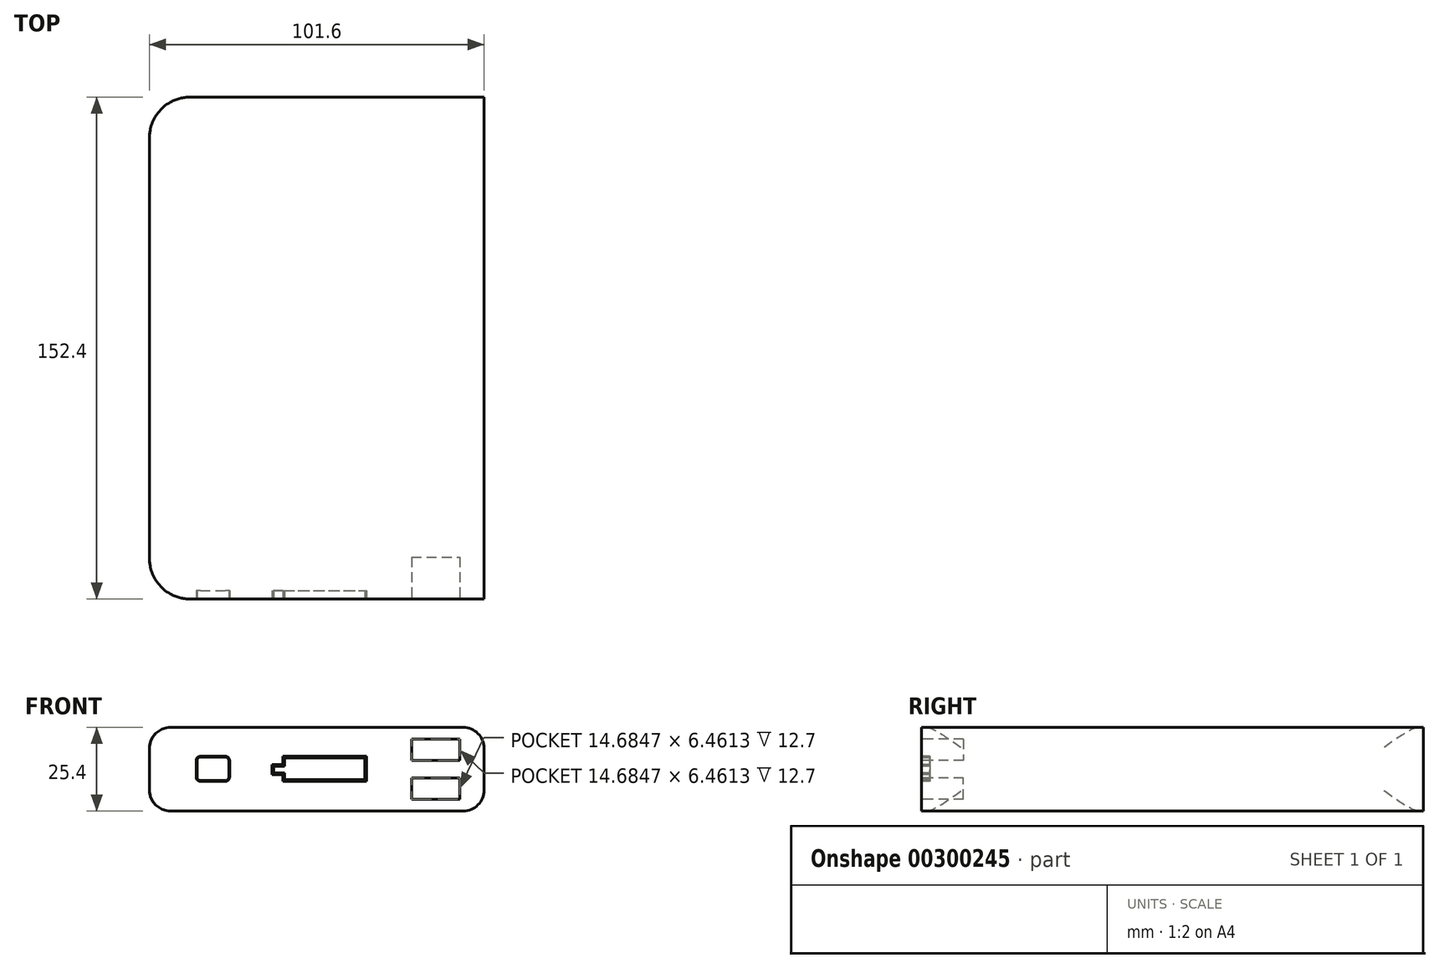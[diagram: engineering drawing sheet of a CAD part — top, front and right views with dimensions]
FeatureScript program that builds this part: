
annotation { "Feature Type Name" : "Feature", "Feature Type Description" : "" }
export const myFeature = defineFeature(function(context is Context, id is Id, definition is map)
    precondition{}
    {
        {
            var Q0;
            Q0=qCreatedBy(makeId("Front.planeOp"),FACE);
            var sketch = newSketch(context, id + "F0", { "sketchPlane" : qUnion([Q0])});
            skLineSegment(sketch, "E0", {"start": v(0, 6.35) * mm, "end": v(0, 19.05) * mm});
            skLineSegment(sketch, "E1", {"start": v(6.35, 25.4) * mm, "end": v(95.25, 25.4) * mm});
            skLineSegment(sketch, "E2", {"start": v(101.6, 19.05) * mm, "end": v(101.6, 6.35) * mm});
            skLineSegment(sketch, "E3", {"start": v(95.25, 0) * mm, "end": v(6.35, 0) * mm});
            skPoint(sketch, "E4.visualSharp", {"position": v(101.6, 25.4) * mm});
            skArc(sketch, "E4.filletArc", {"start": v(101.6, 19.05) * mm, "mid": v(99.74, 23.54) * mm, "end": v(95.25, 25.4) * mm});
            skPoint(sketch, "E5.visualSharp", {"position": v(101.6, 0) * mm});
            skArc(sketch, "E5.filletArc", {"start": v(95.25, 0) * mm, "mid": v(99.74, 1.86) * mm, "end": v(101.6, 6.35) * mm});
            skPoint(sketch, "E6.visualSharp", {"position": v(0, 25.4) * mm});
            skArc(sketch, "E6.filletArc", {"start": v(6.35, 25.4) * mm, "mid": v(1.86, 23.54) * mm, "end": v(0, 19.05) * mm});
            skPoint(sketch, "E7.visualSharp", {"position": v(0, 0) * mm});
            skArc(sketch, "E7.filletArc", {"start": v(0, 6.35) * mm, "mid": v(1.86, 1.86) * mm, "end": v(6.35, 0) * mm});
            skSolve(sketch);
        }
        {
            var Q0;
            Q0=makeQuery(id+"F0.imprint","IMPRINT",FACE,{"disambiguationData":[TD([[makeQuery(id+"F0.imprint","IMPRINT",EDGE,{"derivedFrom":sQuery(id+"F0.wireOp",EDGE,"E0")}),-1.0]])]});
            extrude(context, id + "F1", {"entities" : qUnion([Q0]), "depth" : 152.4 * mm});
        }
        {
            var Q0;
            Q0=makeQuery(id+"F1.opExtrude","CAP_EDGE",EDGE,{"disambiguationData":[OSD([sQuery(id+"F0.wireOp",EDGE,"E0")])],"isStart":false});
            fillet(context, id + "F2", {"entities" : qUnion([Q0]), "radius" : 12.26 * mm, "allowEdgeOverflow" : false});
        }
        {
            var Q0;
            Q0=makeQuery(id+"F1.opExtrude","CAP_EDGE",EDGE,{"disambiguationData":[OSD([sQuery(id+"F0.wireOp",EDGE,"E0")])],"isStart":true});
            fillet(context, id + "F3", {"entities" : qUnion([Q0]), "radius" : 12.27 * mm, "allowEdgeOverflow" : false});
        }
        {
            var Q0;
            Q0=makeQuery(id+"F1.opExtrude","CAP_FACE",FACE,{"disambiguationData":[OSD([sQuery(id+"F0.wireOp",EDGE,"E0"),sQuery(id+"F0.wireOp",EDGE,"E1"),sQuery(id+"F0.wireOp",EDGE,"E2"),sQuery(id+"F0.wireOp",EDGE,"E3"),sQuery(id+"F0.wireOp",EDGE,"E4.filletArc"),sQuery(id+"F0.wireOp",EDGE,"E5.filletArc"),sQuery(id+"F0.wireOp",EDGE,"E6.filletArc"),sQuery(id+"F0.wireOp",EDGE,"E7.filletArc")])],"isStart":false});
            var sketch = newSketch(context, id + "F4", { "sketchPlane" : qUnion([Q0])});
            skLineSegment(sketch, "E8.bottom", {"start": v(79.56, 21.8) * mm, "end": v(94.25, 21.8) * mm});
            skLineSegment(sketch, "E8.top", {"start": v(79.56, 15.34) * mm, "end": v(94.25, 15.34) * mm});
            skLineSegment(sketch, "E8.left", {"start": v(79.56, 21.8) * mm, "end": v(79.56, 15.34) * mm});
            skLineSegment(sketch, "E8.right", {"start": v(94.25, 21.8) * mm, "end": v(94.25, 15.34) * mm});
            skLineSegment(sketch, "E9.MirrorCS", {"start": v(79.56, 3.6) * mm, "end": v(94.25, 3.6) * mm});
            skLineSegment(sketch, "E10.MirrorCS", {"start": v(79.56, 3.6) * mm, "end": v(79.56, 10.06) * mm});
            skLineSegment(sketch, "E11.MirrorCS", {"start": v(79.56, 10.06) * mm, "end": v(94.25, 10.06) * mm});
            skLineSegment(sketch, "E12.MirrorCS", {"start": v(94.25, 3.6) * mm, "end": v(94.25, 10.06) * mm});
            skSolve(sketch);
        }
        {
            var Q0;
            Q0=makeQuery(id+"F4.imprint","IMPRINT",FACE,{"disambiguationData":[TD([[makeQuery(id+"F4.imprint","IMPRINT",EDGE,{"derivedFrom":sQuery(id+"F4.wireOp",EDGE,"E8.bottom")}),-1.0]])]});
            var Q1;
            Q1=makeQuery(id+"F4.imprint","IMPRINT",FACE,{"disambiguationData":[TD([[makeQuery(id+"F4.imprint","IMPRINT",EDGE,{"derivedFrom":sQuery(id+"F4.wireOp",EDGE,"E9.MirrorCS")}),1.0]])]});
            extrude(context, id + "F5", {"entities" : qUnion([Q0, Q1]), "operationType" : NewBodyOperationType.REMOVE, "oppositeDirection" : true, "depth" : 12.7 * mm});
        }
        {
            var Q0;
            Q0=makeQuery(id+"F1.opExtrude","CAP_FACE",FACE,{"disambiguationData":[OSD([sQuery(id+"F0.wireOp",EDGE,"E0"),sQuery(id+"F0.wireOp",EDGE,"E1"),sQuery(id+"F0.wireOp",EDGE,"E2"),sQuery(id+"F0.wireOp",EDGE,"E3"),sQuery(id+"F0.wireOp",EDGE,"E4.filletArc"),sQuery(id+"F0.wireOp",EDGE,"E5.filletArc"),sQuery(id+"F0.wireOp",EDGE,"E6.filletArc"),sQuery(id+"F0.wireOp",EDGE,"E7.filletArc")])],"isStart":false});
            var sketch = newSketch(context, id + "F6", { "sketchPlane" : qUnion([Q0])});
            skLineSegment(sketch, "E13", {"start": v(37.21, 14.1) * mm, "end": v(37.21, 11.05) * mm});
            skLineSegment(sketch, "E14", {"start": v(37.21, 11.05) * mm, "end": v(40.52, 11.05) * mm});
            skLineSegment(sketch, "E15", {"start": v(40.52, 11.05) * mm, "end": v(40.52, 9) * mm});
            skLineSegment(sketch, "E16", {"start": v(40.52, 9) * mm, "end": v(65.92, 9) * mm});
            skLineSegment(sketch, "E17", {"start": v(65.92, 9) * mm, "end": v(65.92, 16.63) * mm});
            skLineSegment(sketch, "E18", {"start": v(65.92, 16.63) * mm, "end": v(40.52, 16.63) * mm});
            skLineSegment(sketch, "E19", {"start": v(40.52, 16.63) * mm, "end": v(40.52, 14.1) * mm});
            skLineSegment(sketch, "E20", {"start": v(40.52, 14.1) * mm, "end": v(37.21, 14.1) * mm});
            skLineSegment(sketch, "E21.0", {"start": v(65.4, 9.51) * mm, "end": v(65.4, 16.12) * mm});
            skLineSegment(sketch, "E21.1", {"start": v(41.02, 9.51) * mm, "end": v(65.4, 9.51) * mm});
            skLineSegment(sketch, "E21.2", {"start": v(65.4, 16.12) * mm, "end": v(41.02, 16.12) * mm});
            skLineSegment(sketch, "E21.3", {"start": v(41.02, 11.56) * mm, "end": v(41.02, 9.51) * mm});
            skLineSegment(sketch, "E21.4", {"start": v(41.02, 16.12) * mm, "end": v(41.02, 13.59) * mm});
            skLineSegment(sketch, "E21.5", {"start": v(41.02, 13.59) * mm, "end": v(37.72, 13.59) * mm});
            skLineSegment(sketch, "E21.6", {"start": v(37.72, 13.59) * mm, "end": v(37.72, 11.56) * mm});
            skLineSegment(sketch, "E21.7", {"start": v(37.72, 11.56) * mm, "end": v(41.02, 11.56) * mm});
            skSolve(sketch);
        }
        {
            var Q0;
            Q0 = qSketchRegion(id + "F6", true);
            extrude(context, id + "F7", {"entities" : qUnion([Q0]), "operationType" : NewBodyOperationType.REMOVE, "oppositeDirection" : true, "depth" : 2.54 * mm});
        }
        {
            var Q0;
            {var subQ0=sQuery(id+"F0.wireOp",EDGE,"E5.filletArc");var subQ1=sQuery(id+"F0.wireOp",EDGE,"E1");var subQ2=sQuery(id+"F0.wireOp",EDGE,"E0");var subQ3=sQuery(id+"F0.wireOp",EDGE,"E2");var subQ4=sQuery(id+"F0.wireOp",EDGE,"E3");var subQ5=sQuery(id+"F0.wireOp",EDGE,"E4.filletArc");Q0=makeQuery(id+"F7.boolean.opBoolean","SPLIT",FACE,{"disambiguationData":[TD([makeQuery(id+"F1.opExtrude","SWEPT_FACE",FACE,{"disambiguationData":[OSD([subQ1])]})])],"derivedFrom":makeQuery(id+"F1.opExtrude","CAP_FACE",FACE,{"disambiguationData":[OSD([subQ2,subQ1,subQ3,subQ4,subQ5,subQ0,sQuery(id+"F0.wireOp",EDGE,"E6.filletArc"),sQuery(id+"F0.wireOp",EDGE,"E7.filletArc")])],"isStart":false})});}
            var sketch = newSketch(context, id + "F8", { "sketchPlane" : qUnion([Q0])});
            skLineSegment(sketch, "E22.bottom", {"start": v(15.44, 16.63) * mm, "end": v(23.06, 16.63) * mm});
            skLineSegment(sketch, "E22.top", {"start": v(15.44, 9) * mm, "end": v(23.06, 9) * mm});
            skLineSegment(sketch, "E22.left", {"start": v(14.17, 15.36) * mm, "end": v(14.17, 10.28) * mm});
            skLineSegment(sketch, "E22.right", {"start": v(24.33, 15.36) * mm, "end": v(24.33, 10.28) * mm});
            skPoint(sketch, "E23.visualSharp", {"position": v(14.17, 16.63) * mm});
            skArc(sketch, "E23.filletArc", {"start": v(15.44, 16.63) * mm, "mid": v(14.54, 16.25) * mm, "end": v(14.17, 15.36) * mm});
            skPoint(sketch, "E24.visualSharp", {"position": v(24.33, 16.63) * mm});
            skArc(sketch, "E24.filletArc", {"start": v(24.33, 15.36) * mm, "mid": v(23.96, 16.25) * mm, "end": v(23.06, 16.63) * mm});
            skPoint(sketch, "E25.visualSharp", {"position": v(24.33, 9) * mm});
            skArc(sketch, "E25.filletArc", {"start": v(23.06, 9) * mm, "mid": v(23.96, 9.38) * mm, "end": v(24.33, 10.28) * mm});
            skPoint(sketch, "E26.visualSharp", {"position": v(14.17, 9) * mm});
            skArc(sketch, "E26.filletArc", {"start": v(14.17, 10.28) * mm, "mid": v(14.54, 9.38) * mm, "end": v(15.44, 9) * mm});
            skArc(sketch, "E27.0", {"start": v(15.44, 16.36) * mm, "mid": v(14.72, 16.07) * mm, "end": v(14.43, 15.36) * mm});
            skLineSegment(sketch, "E27.1", {"start": v(14.43, 15.36) * mm, "end": v(14.43, 10.28) * mm});
            skLineSegment(sketch, "E27.2", {"start": v(15.44, 16.36) * mm, "end": v(23.06, 16.36) * mm});
            skArc(sketch, "E27.3", {"start": v(14.43, 10.28) * mm, "mid": v(14.72, 9.56) * mm, "end": v(15.44, 9.27) * mm});
            skArc(sketch, "E27.4", {"start": v(24.07, 15.36) * mm, "mid": v(23.77, 16.07) * mm, "end": v(23.06, 16.36) * mm});
            skLineSegment(sketch, "E27.5", {"start": v(24.07, 15.36) * mm, "end": v(24.07, 10.28) * mm});
            skArc(sketch, "E27.6", {"start": v(23.06, 9.27) * mm, "mid": v(23.77, 9.56) * mm, "end": v(24.07, 10.28) * mm});
            skLineSegment(sketch, "E27.7", {"start": v(15.44, 9.27) * mm, "end": v(23.06, 9.27) * mm});
            skSolve(sketch);
        }
        {
            var Q0;
            Q0 = qSketchRegion(id + "F8", true);
            extrude(context, id + "F9", {"entities" : qUnion([Q0]), "operationType" : NewBodyOperationType.REMOVE, "oppositeDirection" : true, "depth" : 2.54 * mm});
        }
    });
